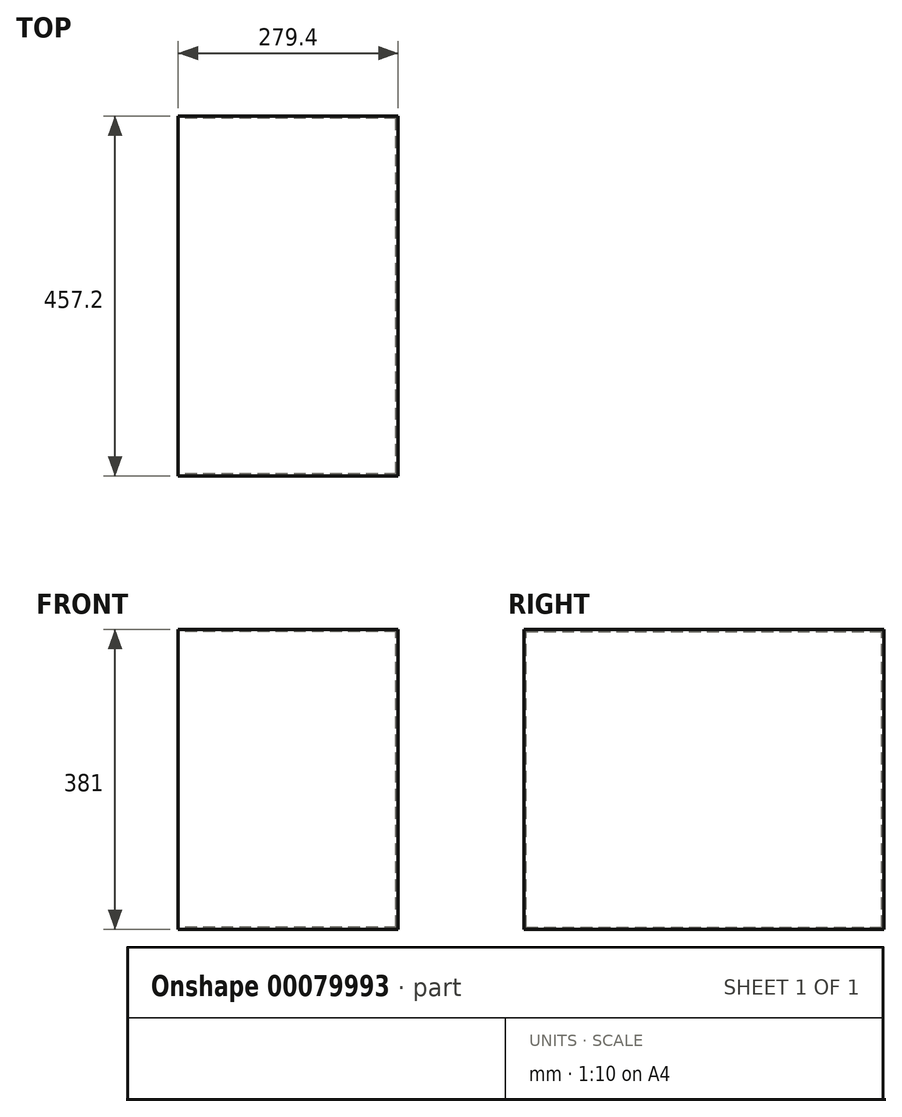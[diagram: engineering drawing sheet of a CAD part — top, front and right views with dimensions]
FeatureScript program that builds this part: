
annotation { "Feature Type Name" : "Feature", "Feature Type Description" : "" }
export const myFeature = defineFeature(function(context is Context, id is Id, definition is map)
    precondition{}
    {
        {
            var Q0;
            Q0=qCreatedBy(makeId("Front.planeOp"),FACE);
            var sketch = newSketch(context, id + "F0", { "sketchPlane" : qUnion([Q0])});
            skLineSegment(sketch, "E0.bottom", {"start": v(139.7, -190.5) * mm, "end": v(-139.7, -190.5) * mm});
            skLineSegment(sketch, "E0.top", {"start": v(139.7, 190.5) * mm, "end": v(-139.7, 190.5) * mm});
            skLineSegment(sketch, "E0.left", {"start": v(139.7, -190.5) * mm, "end": v(139.7, 190.5) * mm});
            skLineSegment(sketch, "E0.right", {"start": v(-139.7, -190.5) * mm, "end": v(-139.7, 190.5) * mm});
            skPoint(sketch, "E0.middle", {"position": v(0, 0) * mm});
            skSolve(sketch);
        }
        {
            var Q0;
            Q0=makeQuery(id+"F0.imprint","IMPRINT",FACE,{"disambiguationData":[TD([[makeQuery(id+"F0.imprint","IMPRINT",EDGE,{"derivedFrom":sQuery(id+"F0.wireOp",EDGE,"E0.bottom")}),-1.0]])]});
            extrude(context, id + "F1", {"entities" : qUnion([Q0]), "endBound" : BoundingType.SYMMETRIC, "depth" : 457.2 * mm});
        }
        {
            var Q0;
            Q0=makeQuery(id+"F1.opExtrude","SWEPT_FACE",FACE,{"disambiguationData":[OSD([sQuery(id+"F0.wireOp",EDGE,"E0.right")])]});
            shell(context, id + "F2", {"entities" : qUnion([Q0]), "thickness" : 2.54 * mm});
        }
    });
